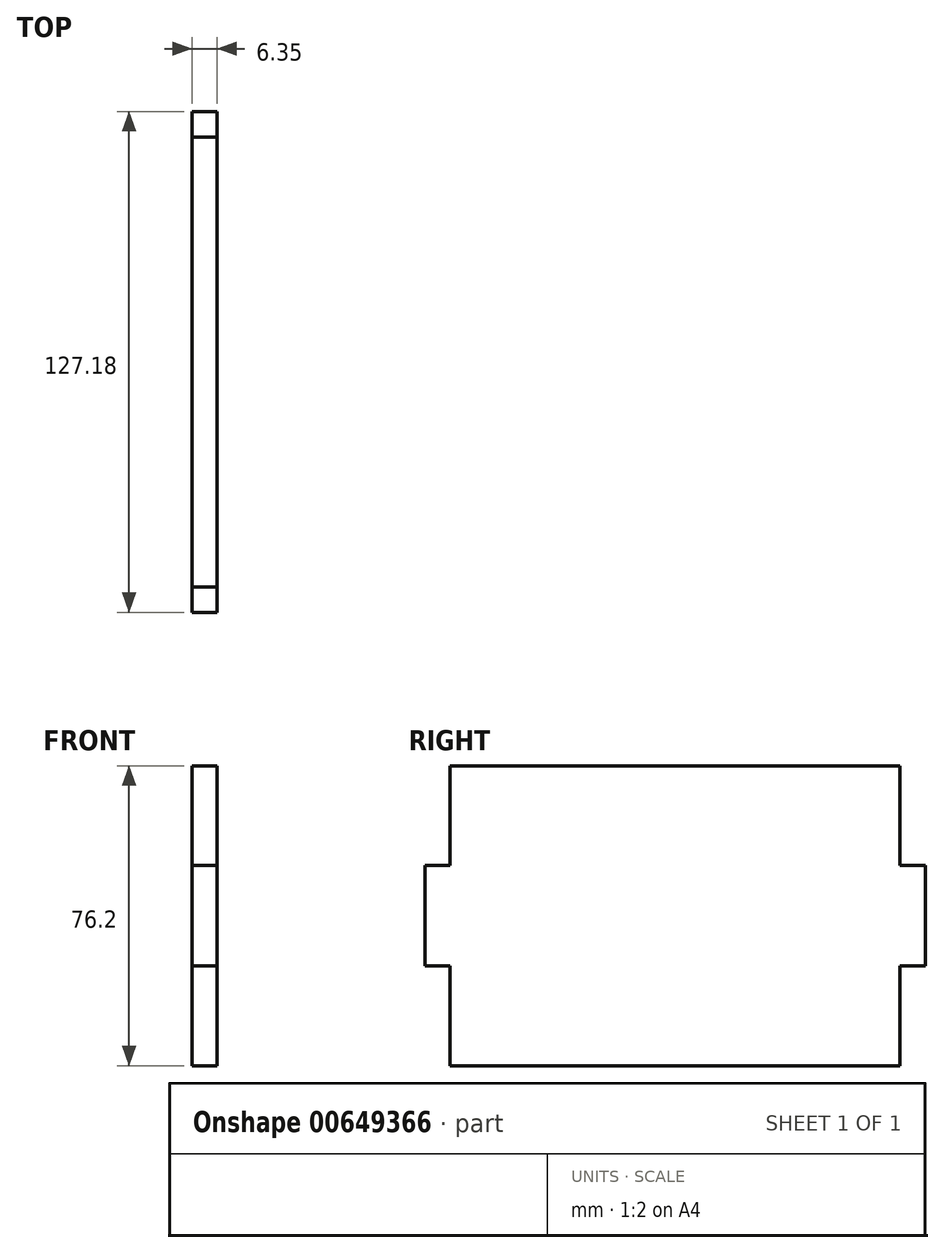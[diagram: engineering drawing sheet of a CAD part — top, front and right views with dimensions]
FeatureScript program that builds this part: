
annotation { "Feature Type Name" : "Feature", "Feature Type Description" : "" }
export const myFeature = defineFeature(function(context is Context, id is Id, definition is map)
    precondition{}
    {
        {
            var Q0;
            Q0=qCreatedBy(makeId("Right.planeOp"),FACE);
            var sketch = newSketch(context, id + "F0", { "sketchPlane" : qUnion([Q0])});
            skLineSegment(sketch, "E0.bottom", {"start": v(0, 0) * mm, "end": v(114.3, 0) * mm});
            skLineSegment(sketch, "E0.top", {"start": v(0, 76.2) * mm, "end": v(114.3, 76.2) * mm});
            skLineSegment(sketch, "E0.left", {"start": v(0, 0) * mm, "end": v(0, 76.2) * mm});
            skLineSegment(sketch, "E0.right", {"start": v(114.3, 0) * mm, "end": v(114.3, 76.2) * mm});
            skLineSegment(sketch, "E1.bottom", {"start": v(0, 50.89) * mm, "end": v(-6.44, 50.89) * mm});
            skLineSegment(sketch, "E1.top", {"start": v(0, 25.31) * mm, "end": v(-6.44, 25.31) * mm});
            skLineSegment(sketch, "E1.left", {"start": v(0, 50.89) * mm, "end": v(0, 25.31) * mm});
            skLineSegment(sketch, "E1.right", {"start": v(-6.44, 50.89) * mm, "end": v(-6.44, 25.31) * mm});
            skLineSegment(sketch, "E2.bottom", {"start": v(114.3, 50.89) * mm, "end": v(120.74, 50.89) * mm});
            skLineSegment(sketch, "E2.top", {"start": v(114.3, 25.31) * mm, "end": v(120.74, 25.31) * mm});
            skLineSegment(sketch, "E2.left", {"start": v(114.3, 50.89) * mm, "end": v(114.3, 25.31) * mm});
            skLineSegment(sketch, "E2.right", {"start": v(120.74, 50.89) * mm, "end": v(120.74, 25.31) * mm});
            skLineSegment(sketch, "E3.bottom", {"start": v(18.96, 0) * mm, "end": v(44.54, 0) * mm});
            skLineSegment(sketch, "E3.top", {"start": v(18.96, -6.44) * mm, "end": v(44.54, -6.44) * mm});
            skLineSegment(sketch, "E3.left", {"start": v(18.96, 0) * mm, "end": v(18.96, -6.44) * mm});
            skLineSegment(sketch, "E3.right", {"start": v(44.54, 0) * mm, "end": v(44.54, -6.44) * mm});
            skLineSegment(sketch, "E4.bottom", {"start": v(69.76, 0) * mm, "end": v(95.34, 0) * mm});
            skLineSegment(sketch, "E4.top", {"start": v(69.76, -6.44) * mm, "end": v(95.34, -6.44) * mm});
            skLineSegment(sketch, "E4.left", {"start": v(69.76, 0) * mm, "end": v(69.76, -6.44) * mm});
            skLineSegment(sketch, "E4.right", {"start": v(95.34, 0) * mm, "end": v(95.34, -6.44) * mm});
            skPoint(sketch, "E5", {"position": v(-6.44, 38.1) * mm});
            skPoint(sketch, "E6", {"position": v(31.75, -6.44) * mm});
            skPoint(sketch, "E7", {"position": v(82.55, -6.44) * mm});
            skSolve(sketch);
        }
        {
            var Q0;
            Q0=makeQuery(id+"F0.imprint","IMPRINT",FACE,{"disambiguationData":[TD([[makeQuery(id+"F0.imprint","IMPRINT",EDGE,{"derivedFrom":sQuery(id+"F0.wireOp",EDGE,"E1.bottom")}),1.0]])]});
            var Q1;
            {var subQ2=sQuery(id+"F0.wireOp",EDGE,"E0.top");Q1=makeQuery(id+"F0.imprint","IMPRINT",FACE,{"disambiguationData":[TD([[makeQuery(id+"F0.imprint","IMPRINT",EDGE,{"derivedFrom":subQ2}),-1.0]])]});}
            var Q2;
            Q2=makeQuery(id+"F0.imprint","IMPRINT",FACE,{"disambiguationData":[TD([[makeQuery(id+"F0.imprint","IMPRINT",EDGE,{"derivedFrom":sQuery(id+"F0.wireOp",EDGE,"E2.bottom")}),-1.0]])]});
            var Q3;
            Q3=makeQuery(id+"F0.imprint","IMPRINT",FACE,{"disambiguationData":[TD([[makeQuery(id+"F0.imprint","IMPRINT",EDGE,{"derivedFrom":sQuery(id+"F0.wireOp",EDGE,"E4.bottom")}),-1.0]])]});
            var Q4;
            Q4=makeQuery(id+"F0.imprint","IMPRINT",FACE,{"disambiguationData":[TD([[makeQuery(id+"F0.imprint","IMPRINT",EDGE,{"derivedFrom":sQuery(id+"F0.wireOp",EDGE,"E3.bottom")}),-1.0]])]});
            extrude(context, id + "F1", {"entities" : qUnion([Q0, Q1, Q2, Q3, Q4]), "depth" : 6.35 * mm, "offsetDistance" : 25.4 * mm});
        }
    });
